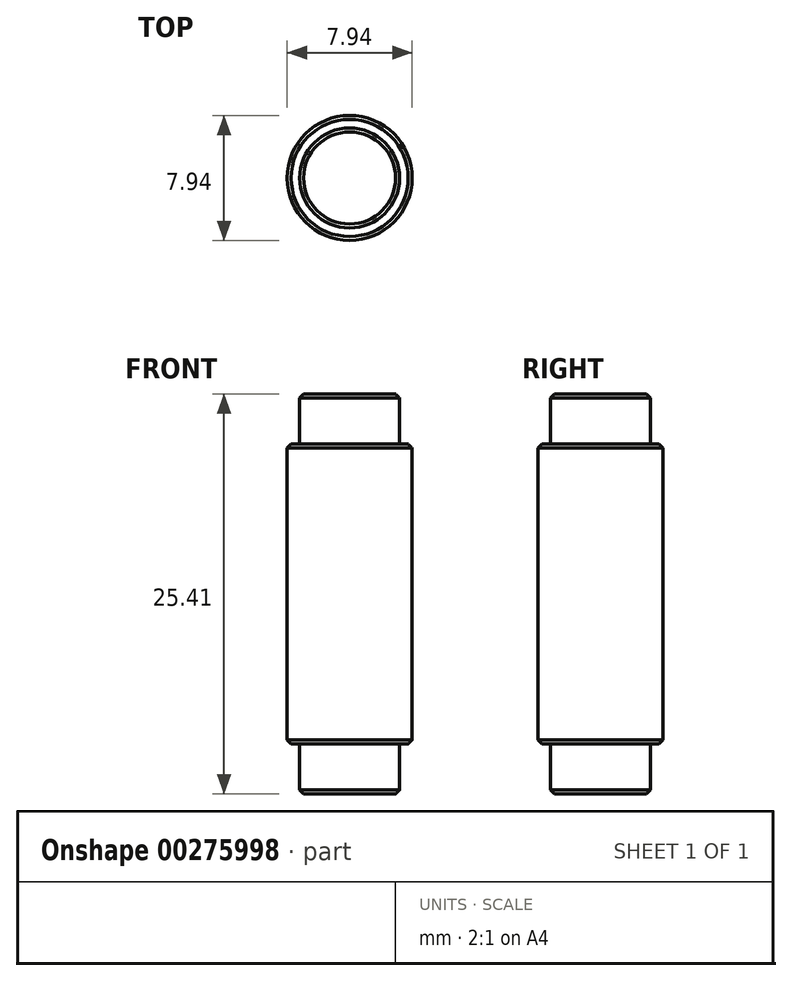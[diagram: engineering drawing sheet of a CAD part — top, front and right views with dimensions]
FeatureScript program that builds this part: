
annotation { "Feature Type Name" : "Feature", "Feature Type Description" : "" }
export const myFeature = defineFeature(function(context is Context, id is Id, definition is map)
    precondition{}
    {
        {
            var Q0;
            Q0=qCreatedBy(makeId("Top.planeOp"),FACE);
            var sketch = newSketch(context, id + "F0", { "sketchPlane" : qUnion([Q0])});
            skCircle(sketch, "E0", {"center": v(0, 0) * mm, "radius": 3.97 * mm});
            skSolve(sketch);
        }
        {
            var Q0;
            Q0=qSketchRegion(id+"F0",true);
            extrude(context, id + "F1", {"entities" : qUnion([Q0]), "depth" : 19.05 * mm});
        }
        {
            var Q0;
            Q0=qCreatedBy(makeId("Top.planeOp"),FACE);
            var sketch = newSketch(context, id + "F2", { "sketchPlane" : qUnion([Q0])});
            skCircle(sketch, "E1", {"center": v(0, 0) * mm, "radius": 3.18 * mm});
            skSolve(sketch);
        }
        {
            var Q0;
            Q0=qSketchRegion(id+"F2",true);
            extrude(context, id + "F3", {"entities" : qUnion([Q0]), "operationType" : NewBodyOperationType.ADD, "oppositeDirection" : true, "depth" : 3.17 * mm});
        }
        {
            var Q0;
            Q0=makeQuery(id+"F1.opExtrude","CAP_FACE",FACE,{"disambiguationData":[OSD([sQuery(id+"F0.wireOp",EDGE,"E0")])],"isStart":false});
            var sketch = newSketch(context, id + "F4", { "sketchPlane" : qUnion([Q0])});
            skCircle(sketch, "E2", {"center": v(0, 0) * mm, "radius": 3.18 * mm});
            skSolve(sketch);
        }
        {
            var Q0;
            Q0=qSketchRegion(id+"F4",true);
            extrude(context, id + "F5", {"entities" : qUnion([Q0]), "operationType" : NewBodyOperationType.ADD, "depth" : 3.17 * mm});
        }
        {
            var Q0;
            Q0=makeQuery(id+"F5.opExtrude","CAP_EDGE",EDGE,{"disambiguationData":[OSD([sQuery(id+"F4.wireOp",EDGE,"E2")])],"isStart":false});
            var Q1;
            Q1=makeQuery(id+"F1.opExtrude","CAP_EDGE",EDGE,{"disambiguationData":[OSD([sQuery(id+"F0.wireOp",EDGE,"E0")])],"isStart":false});
            var Q2;
            Q2=makeQuery(id+"F3.opExtrude","CAP_EDGE",EDGE,{"disambiguationData":[OSD([sQuery(id+"F2.wireOp",EDGE,"E1")])],"isStart":false});
            var Q3;
            Q3=makeQuery(id+"F1.opExtrude","CAP_EDGE",EDGE,{"disambiguationData":[OSD([sQuery(id+"F0.wireOp",EDGE,"E0")])],"isStart":true});
            chamfer(context, id + "F6", {"entities" : qUnion([Q0, Q1, Q2, Q3]), "width" : 0.25 * mm, "tangentPropagation" : true});
        }
    });
